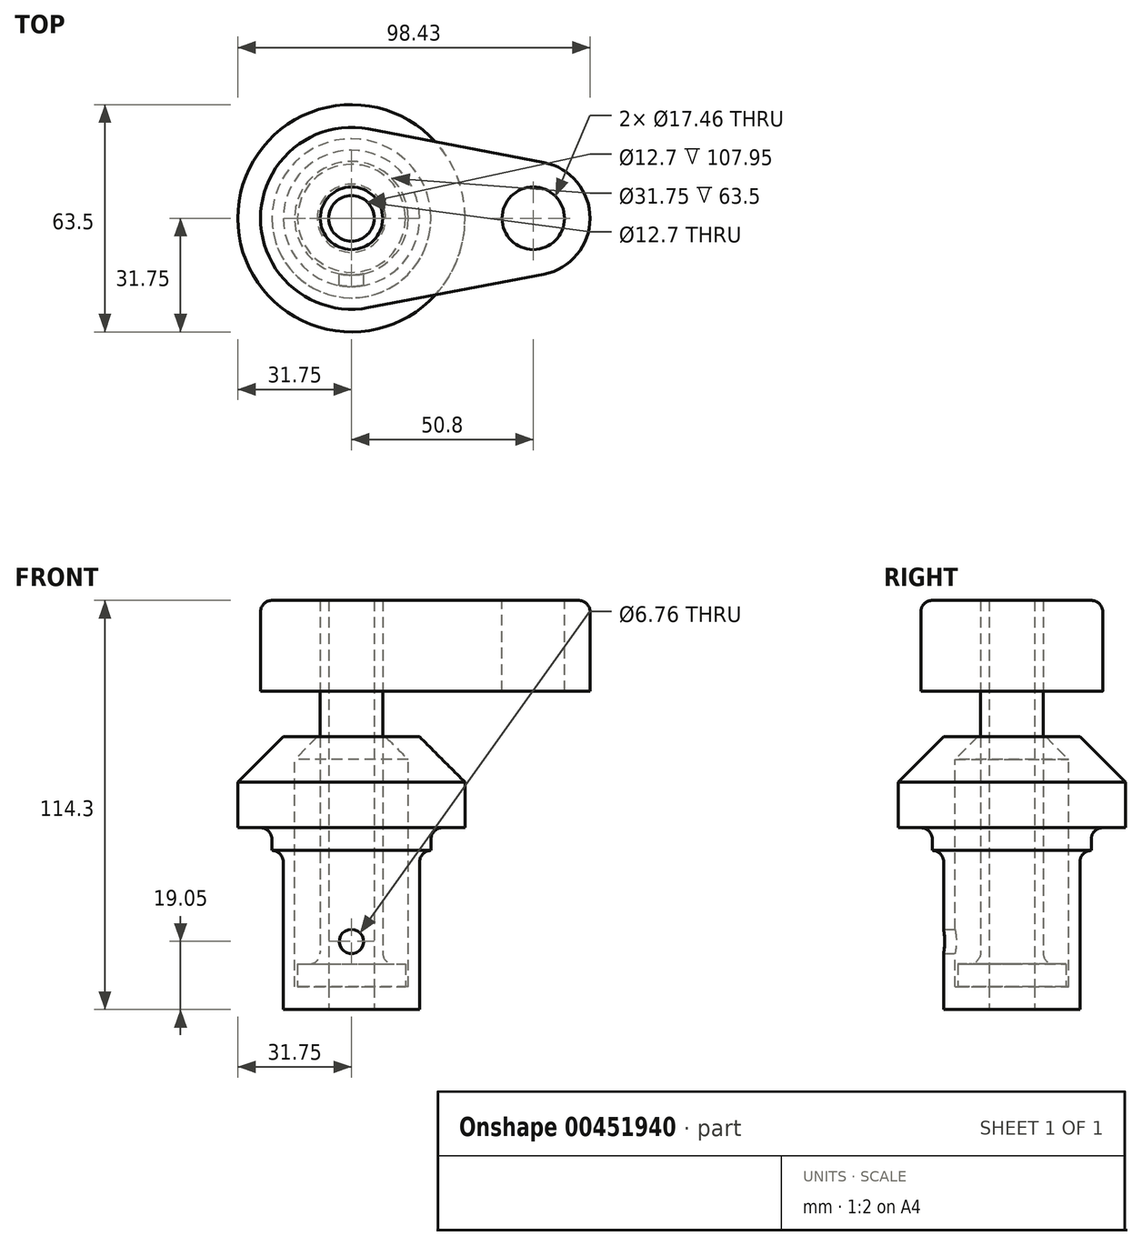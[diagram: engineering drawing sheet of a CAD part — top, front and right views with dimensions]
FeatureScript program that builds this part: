
annotation { "Feature Type Name" : "Feature", "Feature Type Description" : "" }
export const myFeature = defineFeature(function(context is Context, id is Id, definition is map)
    precondition{}
    {
        {
            var Q0;
            Q0=qCreatedBy(makeId("Front.planeOp"),FACE);
            var sketch = newSketch(context, id + "F0", { "sketchPlane" : qUnion([Q0])});
            skLineSegment(sketch, "E0", {"start": v(0, 0) * mm, "end": v(0, 76.2) * mm});
            skLineSegment(sketch, "E1", {"start": v(0, 76.2) * mm, "end": v(19.05, 76.2) * mm});
            skLineSegment(sketch, "E2", {"start": v(19.05, 76.2) * mm, "end": v(31.75, 63.5) * mm});
            skLineSegment(sketch, "E3", {"start": v(31.75, 63.5) * mm, "end": v(31.75, 50.8) * mm});
            skLineSegment(sketch, "E4", {"start": v(31.75, 50.8) * mm, "end": v(22.23, 50.8) * mm});
            skLineSegment(sketch, "E5", {"start": v(22.23, 50.8) * mm, "end": v(22.23, 44.45) * mm});
            skLineSegment(sketch, "E6", {"start": v(22.23, 44.45) * mm, "end": v(19.05, 44.45) * mm});
            skLineSegment(sketch, "E7", {"start": v(19.05, 44.45) * mm, "end": v(19.05, 0) * mm});
            skLineSegment(sketch, "E8", {"start": v(19.05, 0) * mm, "end": v(0, 0) * mm});
            skLineSegment(sketch, "E9", {"start": v(0, 6.35) * mm, "end": v(15.88, 6.35) * mm});
            skLineSegment(sketch, "E10", {"start": v(15.88, 6.35) * mm, "end": v(15.88, 69.85) * mm});
            skLineSegment(sketch, "E11", {"start": v(15.88, 69.85) * mm, "end": v(9.52, 76.2) * mm});
            skLineSegment(sketch, "E12", {"start": v(0, 76.2) * mm, "end": v(0, 120.04) * mm, "construction": true});
            skLineSegment(sketch, "E13", {"start": v(0, 76.2) * mm, "end": v(0, 114.3) * mm});
            skPoint(sketch, "E13.endSnap0", {"position": v(0, 98.12) * mm});
            skLineSegment(sketch, "E14", {"start": v(0, 114.3) * mm, "end": v(8.73, 114.3) * mm});
            skLineSegment(sketch, "E15", {"start": v(8.73, 114.3) * mm, "end": v(8.73, 12.7) * mm});
            skLineSegment(sketch, "E16", {"start": v(8.73, 12.7) * mm, "end": v(15.08, 12.7) * mm});
            skLineSegment(sketch, "E17", {"start": v(15.08, 12.7) * mm, "end": v(15.08, 6.35) * mm});
            skSolve(sketch);
        }
        {
            var Q0;
            {var subQ3=sQuery(id+"F0.wireOp",EDGE,"E2");Q0=makeQuery(id+"F0.imprint","IMPRINT",FACE,{"disambiguationData":[TD([[makeQuery(id+"F0.imprint","IMPRINT",EDGE,{"derivedFrom":subQ3}),-1.0]])]});}
            var Q1;
            Q1=sQuery(id+"F0.wireOp",EDGE,"E0");
            revolve(context, id + "F1", {"entities" : qUnion([Q0]), "axis" : qUnion([Q1]), "revolveType" : RevolveType.FULL, "oppositeDirection" : true});
        }
        {
            var Q0;
            {var subQ0=sQuery(id+"F0.wireOp",EDGE,"E13");Q0=makeQuery(id+"F0.imprint","IMPRINT",FACE,{"disambiguationData":[TD([[makeQuery(id+"F0.imprint","IMPRINT",EDGE,{"derivedFrom":subQ0}),-1.0]])]});}
            var Q1;
            {var subQ0=sQuery(id+"F0.wireOp",EDGE,"E16");Q1=makeQuery(id+"F0.imprint","IMPRINT",FACE,{"disambiguationData":[TD([[makeQuery(id+"F0.imprint","IMPRINT",EDGE,{"derivedFrom":subQ0}),-1.0]])]});}
            var Q2;
            Q2=sQuery(id+"F0.wireOp",EDGE,"E13");
            revolve(context, id + "F2", {"entities" : qUnion([Q0, Q1]), "axis" : qUnion([Q2]), "revolveType" : RevolveType.FULL});
        }
        {
            var Q0;
            Q0=makeQuery(id+"F2.opRevolve","SWEPT_FACE",FACE,{"disambiguationData":[OSD([sQuery(id+"F0.wireOp",EDGE,"E14")])]});
            var sketch = newSketch(context, id + "F3", { "sketchPlane" : qUnion([Q0])});
            skCircle(sketch, "E18", {"center": v(0, 0) * mm, "radius": 25.4 * mm});
            skCircle(sketch, "E19", {"center": v(50.8, 0) * mm, "radius": 15.88 * mm});
            skLineSegment(sketch, "E20", {"start": v(4.76, 24.95) * mm, "end": v(53.78, 15.6) * mm});
            skLineSegment(sketch, "E21", {"start": v(53.78, -15.6) * mm, "end": v(4.76, -24.95) * mm});
            skCircle(sketch, "E22.0", {"center": v(0, 0) * mm, "radius": 8.73 * mm});
            skCircle(sketch, "E23", {"center": v(50.8, 0) * mm, "radius": 8.73 * mm});
            skSolve(sketch);
        }
        {
            var Q0;
            Q0 = qSketchRegion(id + "F3", true);
            var Q1;
            Q1=makeQuery(id+"F1.opRevolve","SWEPT_FACE",FACE,{"disambiguationData":[OSD([sQuery(id+"F0.wireOp",EDGE,"E1")])]});
            extrude(context, id + "F4", {"entities" : qUnion([Q0]), "oppositeDirection" : true, "endBoundEntityFace" : qUnion([Q1]), "depth" : 25.4 * mm});
        }
        {
            var Q0;
            Q0=qCreatedBy(makeId("Front.planeOp"),FACE);
            var sketch = newSketch(context, id + "F5", { "sketchPlane" : qUnion([Q0])});
            skPoint(sketch, "E24", {"position": v(0, 19.05) * mm});
            skSolve(sketch);
        }
        {
            var Q0;
            Q0=sQuery(id+"F5.wireOp",VERTEX,"E24");
            var Q1;
            Q1=makeQuery(id+"F1.opRevolve","SWEPT_BODY",BODY,{"disambiguationData":[OSD([sQuery(id+"F0.wireOp",EDGE,"E0"),sQuery(id+"F0.wireOp",EDGE,"E1"),sQuery(id+"F0.wireOp",EDGE,"E2"),sQuery(id+"F0.wireOp",EDGE,"E3"),sQuery(id+"F0.wireOp",EDGE,"E4"),sQuery(id+"F0.wireOp",EDGE,"E5"),sQuery(id+"F0.wireOp",EDGE,"E6"),sQuery(id+"F0.wireOp",EDGE,"E7"),sQuery(id+"F0.wireOp",EDGE,"E8"),sQuery(id+"F0.wireOp",EDGE,"E9"),sQuery(id+"F0.wireOp",EDGE,"E10"),sQuery(id+"F0.wireOp",EDGE,"E11")])]});
            hole(context, id + "F6", {"style" : HoleStyle.SIMPLE, "endStyle" : HoleEndStyle.THROUGH, "oppositeDirection" : true, "standardTappedOrClearance" : lookupTablePath({ "standard" : "ANSI", "fit" : "Normal (ASME)", "size" : "1/4", "type" : "Clearance" }), "standardBlindInLast" : lookupTablePath({ "fit" : "Free", "standard" : "ANSI", "size" : "1/4", "type" : "Clearance" }), "holeDiameter" : 6.76 * mm, "isTappedThrough" : true, "tappedDepth" : 8.9 * mm, "tapClearance" : 3, "locations" : qUnion([Q0]), "scope" : qUnion([Q1])});
        }
        {
            var Q0;
            Q0=makeQuery(id+"F4.opExtrude","CAP_EDGE",EDGE,{"disambiguationData":[OSD([sQuery(id+"F3.wireOp",EDGE,"E20")])],"isStart":true});
            var Q1;
            Q1=makeQuery(id+"F1.opRevolve","SWEPT_EDGE",EDGE,{"disambiguationData":[OSD([sQuery(id+"F0.wireOp",EDGE,"E6"),sQuery(id+"F0.wireOp",EDGE,"E7")])]});
            var Q2;
            Q2=makeQuery(id+"F1.opRevolve","SWEPT_EDGE",EDGE,{"disambiguationData":[OSD([sQuery(id+"F0.wireOp",EDGE,"E4"),sQuery(id+"F0.wireOp",EDGE,"E5")])]});
            var Q3;
            Q3=makeQuery(id+"F2.opRevolve","SWEPT_EDGE",EDGE,{"disambiguationData":[OSD([sQuery(id+"F0.wireOp",EDGE,"E15"),sQuery(id+"F0.wireOp",EDGE,"E16")])]});
            fillet(context, id + "F7", {"entities" : qUnion([Q0, Q1, Q2, Q3]), "radius" : 3.17 * mm, "tangentPropagation" : true, "allowEdgeOverflow" : false});
        }
        {
            var Q0;
            Q0=makeQuery(id+"F1.opRevolve","SWEPT_FACE",FACE,{"disambiguationData":[OSD([sQuery(id+"F0.wireOp",EDGE,"E8")])]});
            var sketch = newSketch(context, id + "F8", { "sketchPlane" : qUnion([Q0])});
            skCircle(sketch, "E25", {"center": v(0, 0) * mm, "radius": 6.35 * mm});
            skSolve(sketch);
        }
        {
            var Q0;
            Q0=makeQuery(id+"F8.imprint","IMPRINT",FACE,{"disambiguationData":[TD([[makeQuery(id+"F8.imprint","IMPRINT",EDGE,{"derivedFrom":sQuery(id+"F8.wireOp",EDGE,"E25")}),1.0]])]});
            extrude(context, id + "F9", {"entities" : qUnion([Q0]), "operationType" : NewBodyOperationType.REMOVE, "endBound" : BoundingType.THROUGH_ALL, "oppositeDirection" : true, "depth" : 25.4 * mm});
        }
    });
